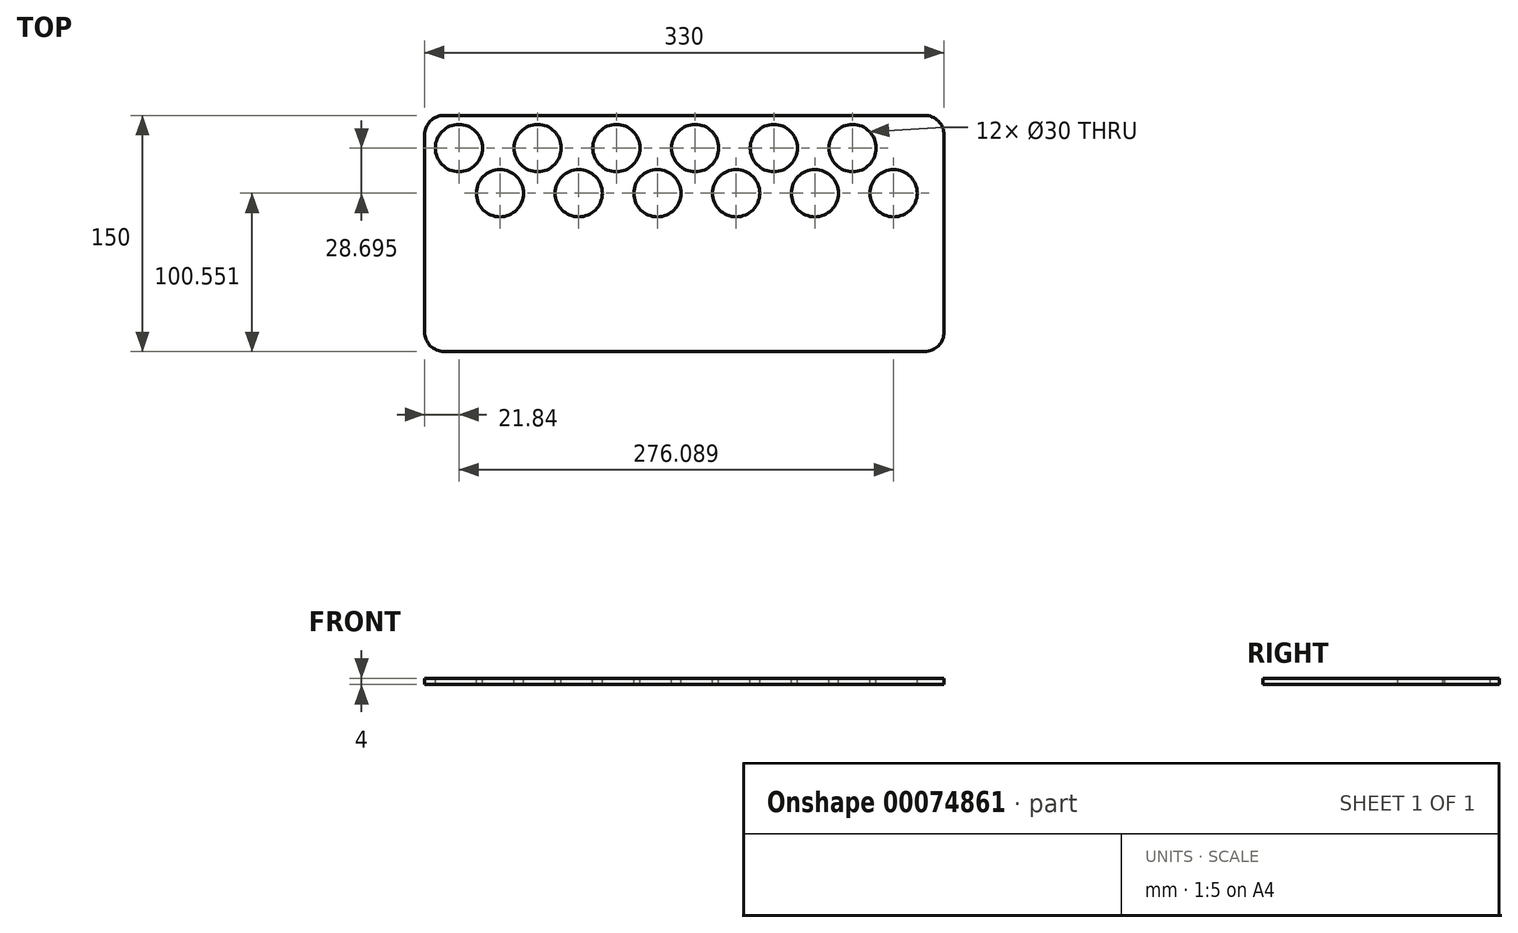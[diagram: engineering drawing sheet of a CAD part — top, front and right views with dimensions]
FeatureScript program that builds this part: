
annotation { "Feature Type Name" : "Feature", "Feature Type Description" : "" }
export const myFeature = defineFeature(function(context is Context, id is Id, definition is map)
    precondition{}
    {
        {
            var Q0;
            Q0=qCreatedBy(makeId("Top.planeOp"),FACE);
            var sketch = newSketch(context, id + "F0", { "sketchPlane" : qUnion([Q0])});
            skLineSegment(sketch, "E0.bottom", {"start": v(12.5, 0) * mm, "end": v(317.5, 0) * mm});
            skLineSegment(sketch, "E0.top", {"start": v(12.5, 150) * mm, "end": v(317.5, 150) * mm});
            skLineSegment(sketch, "E0.left", {"start": v(0, 12.5) * mm, "end": v(0, 137.5) * mm});
            skLineSegment(sketch, "E0.right", {"start": v(330, 12.5) * mm, "end": v(330, 137.5) * mm});
            skPoint(sketch, "E1.visualSharp", {"position": v(0, 150) * mm});
            skArc(sketch, "E1.filletArc", {"start": v(12.5, 150) * mm, "mid": v(3.66, 146.34) * mm, "end": v(0, 137.5) * mm});
            skPoint(sketch, "E2.visualSharp", {"position": v(0, 0) * mm});
            skArc(sketch, "E2.filletArc", {"start": v(0, 12.5) * mm, "mid": v(3.66, 3.66) * mm, "end": v(12.5, 0) * mm});
            skPoint(sketch, "E3.visualSharp", {"position": v(330, 0) * mm});
            skArc(sketch, "E3.filletArc", {"start": v(317.5, 0) * mm, "mid": v(326.34, 3.66) * mm, "end": v(330, 12.5) * mm});
            skPoint(sketch, "E4.visualSharp", {"position": v(330, 150) * mm});
            skArc(sketch, "E4.filletArc", {"start": v(330, 137.5) * mm, "mid": v(326.34, 146.34) * mm, "end": v(317.5, 150) * mm});
            skSolve(sketch);
        }
        {
            var Q0;
            Q0=makeQuery(id+"F0.imprint","IMPRINT",FACE,{"disambiguationData":[TD([[makeQuery(id+"F0.imprint","IMPRINT",EDGE,{"derivedFrom":sQuery(id+"F0.wireOp",EDGE,"E0.bottom")}),1.0]])]});
            extrude(context, id + "F1", {"entities" : qUnion([Q0]), "depth" : 4 * mm});
        }
        {
            var Q0;
            Q0=makeQuery(id+"F1.opExtrude","CAP_FACE",FACE,{"disambiguationData":[OSD([sQuery(id+"F0.wireOp",EDGE,"E0.bottom"),sQuery(id+"F0.wireOp",EDGE,"E0.top"),sQuery(id+"F0.wireOp",EDGE,"E0.left"),sQuery(id+"F0.wireOp",EDGE,"E0.right"),sQuery(id+"F0.wireOp",EDGE,"E1.filletArc"),sQuery(id+"F0.wireOp",EDGE,"E2.filletArc"),sQuery(id+"F0.wireOp",EDGE,"E3.filletArc"),sQuery(id+"F0.wireOp",EDGE,"E4.filletArc")])],"isStart":false});
            var sketch = newSketch(context, id + "F2", { "sketchPlane" : qUnion([Q0])});
            skLineSegment(sketch, "E5.0", {"start": v(12.5, 75) * mm, "end": v(317.5, 75) * mm, "construction": true});
            skCircle(sketch, "E6", {"center": v(21.84, 129.25) * mm, "radius": 15 * mm});
            skLineSegment(sketch, "E7", {"start": v(21.84, 129.25) * mm, "end": v(271.84, 129.25) * mm, "construction": true});
            skCircle(sketch, "E8.0.1.0", {"center": v(47.93, 100.55) * mm, "radius": 15 * mm});
            skCircle(sketch, "E8.1.0.0", {"center": v(71.84, 129.25) * mm, "radius": 15 * mm});
            skCircle(sketch, "E8.1.1.0", {"center": v(97.93, 100.55) * mm, "radius": 15 * mm});
            skCircle(sketch, "E8.2.0.0", {"center": v(121.84, 129.25) * mm, "radius": 15 * mm});
            skCircle(sketch, "E8.2.1.0", {"center": v(147.93, 100.55) * mm, "radius": 15 * mm});
            skCircle(sketch, "E8.3.0.0", {"center": v(171.84, 129.25) * mm, "radius": 15 * mm});
            skCircle(sketch, "E8.3.1.0", {"center": v(197.93, 100.55) * mm, "radius": 15 * mm});
            skCircle(sketch, "E8.4.0.0", {"center": v(221.84, 129.25) * mm, "radius": 15 * mm});
            skCircle(sketch, "E8.4.1.0", {"center": v(247.93, 100.55) * mm, "radius": 15 * mm});
            skCircle(sketch, "E8.5.0.0", {"center": v(271.84, 129.25) * mm, "radius": 15 * mm});
            skCircle(sketch, "E8.5.1.0", {"center": v(297.93, 100.55) * mm, "radius": 15 * mm});
            skLineSegment(sketch, "E8.direction1", {"start": v(21.84, 129.25) * mm, "end": v(71.84, 129.25) * mm, "construction": true});
            skLineSegment(sketch, "E8.direction2", {"start": v(21.84, 129.25) * mm, "end": v(47.93, 100.55) * mm, "construction": true});
            skSolve(sketch);
        }
        {
            var Q0;
            Q0=makeQuery(id+"F2.imprint","IMPRINT",FACE,{"disambiguationData":[TD([[makeQuery(id+"F2.imprint","IMPRINT",EDGE,{"derivedFrom":sQuery(id+"F2.wireOp",EDGE,"E6")}),1.0]])]});
            var Q1;
            Q1=makeQuery(id+"F2.imprint","IMPRINT",FACE,{"disambiguationData":[TD([[makeQuery(id+"F2.imprint","IMPRINT",EDGE,{"derivedFrom":sQuery(id+"F2.wireOp",EDGE,"E8.1.0.0")}),1.0]])]});
            var Q2;
            Q2=makeQuery(id+"F2.imprint","IMPRINT",FACE,{"disambiguationData":[TD([[makeQuery(id+"F2.imprint","IMPRINT",EDGE,{"derivedFrom":sQuery(id+"F2.wireOp",EDGE,"E8.2.0.0")}),1.0]])]});
            var Q3;
            Q3=makeQuery(id+"F2.imprint","IMPRINT",FACE,{"disambiguationData":[TD([[makeQuery(id+"F2.imprint","IMPRINT",EDGE,{"derivedFrom":sQuery(id+"F2.wireOp",EDGE,"E8.3.0.0")}),1.0]])]});
            var Q4;
            Q4=makeQuery(id+"F2.imprint","IMPRINT",FACE,{"disambiguationData":[TD([[makeQuery(id+"F2.imprint","IMPRINT",EDGE,{"derivedFrom":sQuery(id+"F2.wireOp",EDGE,"E8.4.0.0")}),1.0]])]});
            var Q5;
            Q5=makeQuery(id+"F2.imprint","IMPRINT",FACE,{"disambiguationData":[TD([[makeQuery(id+"F2.imprint","IMPRINT",EDGE,{"derivedFrom":sQuery(id+"F2.wireOp",EDGE,"E8.5.0.0")}),1.0]])]});
            var Q6;
            Q6=makeQuery(id+"F2.imprint","IMPRINT",FACE,{"disambiguationData":[TD([[makeQuery(id+"F2.imprint","IMPRINT",EDGE,{"derivedFrom":sQuery(id+"F2.wireOp",EDGE,"E8.0.1.0")}),1.0]])]});
            var Q7;
            Q7=makeQuery(id+"F2.imprint","IMPRINT",FACE,{"disambiguationData":[TD([[makeQuery(id+"F2.imprint","IMPRINT",EDGE,{"derivedFrom":sQuery(id+"F2.wireOp",EDGE,"E8.1.1.0")}),1.0]])]});
            var Q8;
            Q8=makeQuery(id+"F2.imprint","IMPRINT",FACE,{"disambiguationData":[TD([[makeQuery(id+"F2.imprint","IMPRINT",EDGE,{"derivedFrom":sQuery(id+"F2.wireOp",EDGE,"E8.2.1.0")}),1.0]])]});
            var Q9;
            Q9=makeQuery(id+"F2.imprint","IMPRINT",FACE,{"disambiguationData":[TD([[makeQuery(id+"F2.imprint","IMPRINT",EDGE,{"derivedFrom":sQuery(id+"F2.wireOp",EDGE,"E8.3.1.0")}),1.0]])]});
            var Q10;
            Q10=makeQuery(id+"F2.imprint","IMPRINT",FACE,{"disambiguationData":[TD([[makeQuery(id+"F2.imprint","IMPRINT",EDGE,{"derivedFrom":sQuery(id+"F2.wireOp",EDGE,"E8.4.1.0")}),1.0]])]});
            var Q11;
            Q11=makeQuery(id+"F2.imprint","IMPRINT",FACE,{"disambiguationData":[TD([[makeQuery(id+"F2.imprint","IMPRINT",EDGE,{"derivedFrom":sQuery(id+"F2.wireOp",EDGE,"E8.5.1.0")}),1.0]])]});
            extrude(context, id + "F3", {"entities" : qUnion([Q0, Q1, Q2, Q3, Q4, Q5, Q6, Q7, Q8, Q9, Q10, Q11]), "operationType" : NewBodyOperationType.REMOVE, "oppositeDirection" : true, "depth" : 25 * mm});
        }
    });
